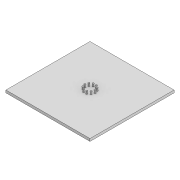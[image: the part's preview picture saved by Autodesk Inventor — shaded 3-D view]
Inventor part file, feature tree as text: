
AUTODESK INVENTOR PART (.ipt)
format: ipt  version: 2021 (Build 250183000, 183)  size: 98,304 bytes
history: native  units: in
note: dims shown in document units (in); Inventor stores cm internally (conversion verified against a paired STEP export)
features: extrude x2, sketch x2
ambient origin geometry x8: Origin, YZ Plane, XZ Plane, XY Plane, X Axis, Y Axis, Z Axis, Center Point
bodies: Solid1 (feature_tree)
feature tree (4):
  extrude  "Extrusion1"  Depth=3937.0079in
  extrude  "Extrusion2"  Depth=118.1102in
  sketch  "Sketch1"  dims[d0=3937.0079in d1=3937.0079in]
  sketch  "Sketch2"  dims[d2=118.1102in d3=0.0in d4=472.4409in d5=78.7402in d6=3.937in d8=360.0deg d10=118.1102in d11=0.0in]
